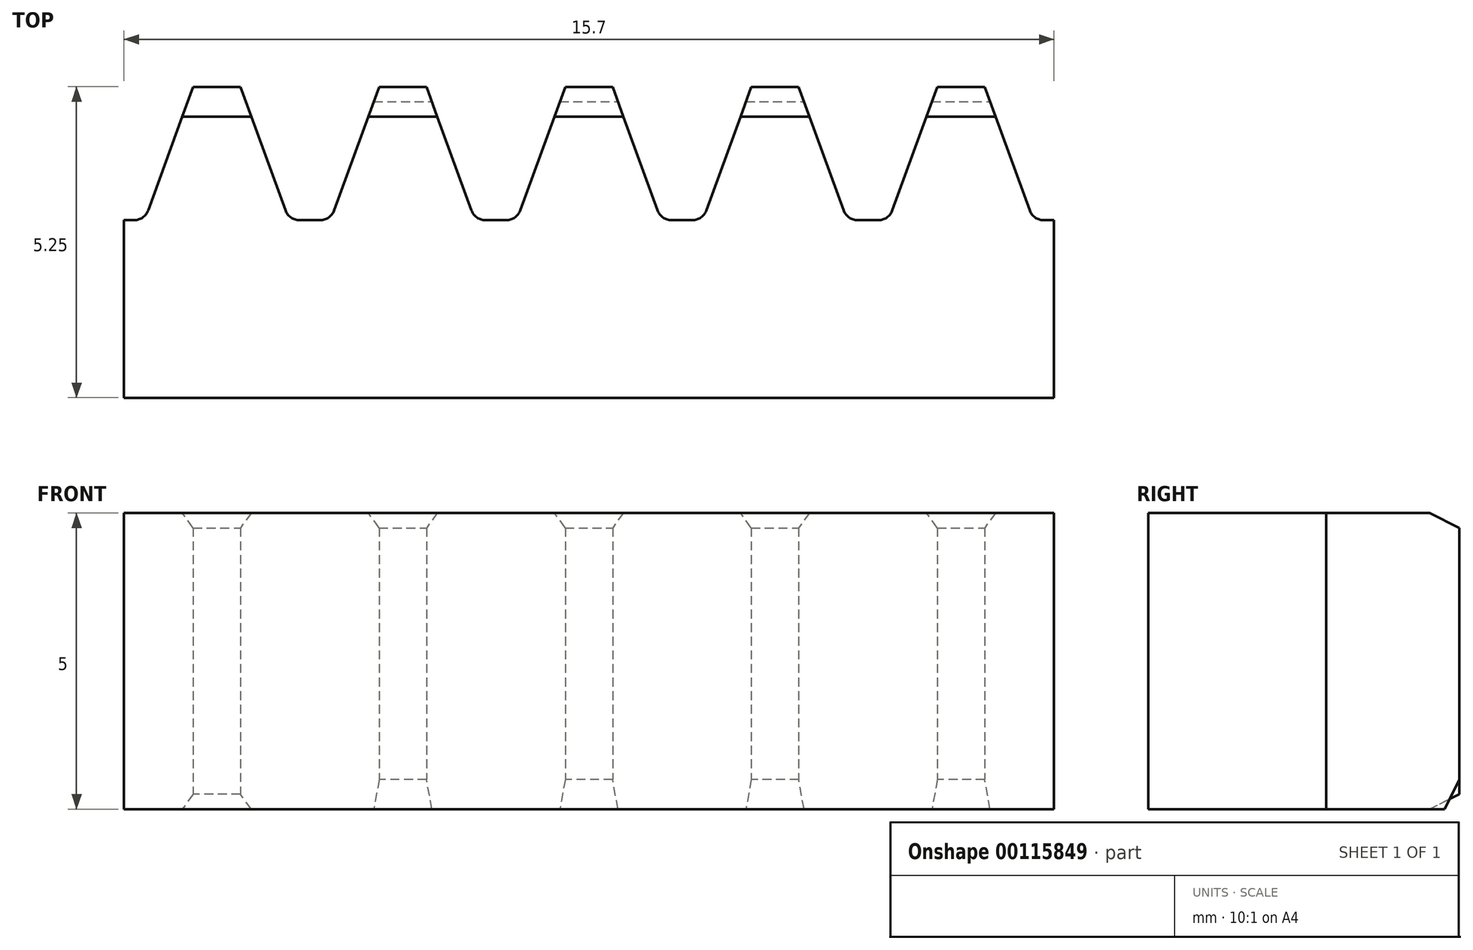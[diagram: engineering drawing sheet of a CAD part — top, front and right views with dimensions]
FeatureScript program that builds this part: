
annotation { "Feature Type Name" : "Feature", "Feature Type Description" : "" }
export const myFeature = defineFeature(function(context is Context, id is Id, definition is map)
    precondition{}
    {
        {
            var Q0;
            Q0=qCreatedBy(makeId("Top.planeOp"),FACE);
            var sketch = newSketch(context, id + "F0", { "sketchPlane" : qUnion([Q0])});
            skLineSegment(sketch, "E0", {"start": v(0.48, -14.18) * mm, "end": v(1.24, -12.1) * mm});
            skLineSegment(sketch, "E1", {"start": v(1.24, -12.1) * mm, "end": v(2.04, -12.1) * mm});
            skLineSegment(sketch, "E2", {"start": v(2.04, -12.1) * mm, "end": v(2.8, -14.18) * mm});
            skLineSegment(sketch, "E3", {"start": v(3.03, -14.34) * mm, "end": v(3.38, -14.34) * mm});
            skLineSegment(sketch, "E4", {"start": v(3.62, -14.18) * mm, "end": v(4.38, -12.1) * mm});
            skLineSegment(sketch, "E5", {"start": v(4.38, -12.1) * mm, "end": v(5.18, -12.1) * mm});
            skLineSegment(sketch, "E6", {"start": v(5.18, -12.1) * mm, "end": v(5.94, -14.18) * mm});
            skLineSegment(sketch, "E7", {"start": v(6.17, -14.34) * mm, "end": v(6.53, -14.34) * mm});
            skLineSegment(sketch, "E8", {"start": v(6.76, -14.18) * mm, "end": v(7.52, -12.1) * mm});
            skLineSegment(sketch, "E9", {"start": v(7.52, -12.1) * mm, "end": v(8.32, -12.1) * mm});
            skLineSegment(sketch, "E10", {"start": v(8.32, -12.1) * mm, "end": v(9.08, -14.18) * mm});
            skLineSegment(sketch, "E11", {"start": v(9.31, -14.34) * mm, "end": v(9.67, -14.34) * mm});
            skLineSegment(sketch, "E12", {"start": v(9.9, -14.18) * mm, "end": v(10.66, -12.1) * mm});
            skLineSegment(sketch, "E13", {"start": v(10.66, -12.1) * mm, "end": v(11.46, -12.1) * mm});
            skLineSegment(sketch, "E14", {"start": v(11.46, -12.1) * mm, "end": v(12.22, -14.18) * mm});
            skLineSegment(sketch, "E15", {"start": v(12.46, -14.34) * mm, "end": v(12.8, -14.34) * mm});
            skLineSegment(sketch, "E16", {"start": v(13.04, -14.18) * mm, "end": v(13.8, -12.1) * mm});
            skLineSegment(sketch, "E17", {"start": v(13.8, -12.1) * mm, "end": v(14.6, -12.1) * mm});
            skLineSegment(sketch, "E18", {"start": v(14.6, -12.1) * mm, "end": v(15.36, -14.18) * mm});
            skLineSegment(sketch, "E19", {"start": v(0.07, -14.34) * mm, "end": v(0.07, -17.34) * mm});
            skLineSegment(sketch, "E20", {"start": v(15.77, -14.34) * mm, "end": v(15.77, -17.34) * mm});
            skLineSegment(sketch, "E21", {"start": v(0.07, -14.34) * mm, "end": v(0.24, -14.34) * mm});
            skLineSegment(sketch, "E22", {"start": v(0.07, -17.34) * mm, "end": v(15.77, -17.34) * mm});
            skLineSegment(sketch, "E23", {"start": v(15.6, -14.34) * mm, "end": v(15.77, -14.34) * mm});
            skPoint(sketch, "E24.visualSharp", {"position": v(0.42, -14.34) * mm});
            skArc(sketch, "E24.filletArc", {"start": v(0.24, -14.34) * mm, "mid": v(0.39, -14.3) * mm, "end": v(0.48, -14.18) * mm});
            skPoint(sketch, "E25.visualSharp", {"position": v(2.86, -14.34) * mm});
            skArc(sketch, "E25.filletArc", {"start": v(2.8, -14.18) * mm, "mid": v(2.89, -14.3) * mm, "end": v(3.03, -14.34) * mm});
            skPoint(sketch, "E26.visualSharp", {"position": v(3.56, -14.34) * mm});
            skArc(sketch, "E26.filletArc", {"start": v(3.38, -14.34) * mm, "mid": v(3.53, -14.3) * mm, "end": v(3.62, -14.18) * mm});
            skPoint(sketch, "E27.visualSharp", {"position": v(6, -14.34) * mm});
            skArc(sketch, "E27.filletArc", {"start": v(5.94, -14.18) * mm, "mid": v(6.03, -14.3) * mm, "end": v(6.17, -14.34) * mm});
            skPoint(sketch, "E28.visualSharp", {"position": v(6.7, -14.34) * mm});
            skArc(sketch, "E28.filletArc", {"start": v(6.53, -14.34) * mm, "mid": v(6.67, -14.3) * mm, "end": v(6.76, -14.18) * mm});
            skPoint(sketch, "E29.visualSharp", {"position": v(9.14, -14.34) * mm});
            skArc(sketch, "E29.filletArc", {"start": v(9.08, -14.18) * mm, "mid": v(9.17, -14.3) * mm, "end": v(9.31, -14.34) * mm});
            skPoint(sketch, "E30.visualSharp", {"position": v(9.84, -14.34) * mm});
            skArc(sketch, "E30.filletArc", {"start": v(9.67, -14.34) * mm, "mid": v(9.81, -14.3) * mm, "end": v(9.9, -14.18) * mm});
            skPoint(sketch, "E31.visualSharp", {"position": v(12.28, -14.34) * mm});
            skArc(sketch, "E31.filletArc", {"start": v(12.22, -14.18) * mm, "mid": v(12.31, -14.3) * mm, "end": v(12.46, -14.34) * mm});
            skPoint(sketch, "E32.visualSharp", {"position": v(12.98, -14.34) * mm});
            skArc(sketch, "E32.filletArc", {"start": v(12.8, -14.34) * mm, "mid": v(12.95, -14.3) * mm, "end": v(13.04, -14.18) * mm});
            skPoint(sketch, "E33.visualSharp", {"position": v(15.42, -14.34) * mm});
            skArc(sketch, "E33.filletArc", {"start": v(15.36, -14.18) * mm, "mid": v(15.45, -14.3) * mm, "end": v(15.6, -14.34) * mm});
            skSolve(sketch);
        }
        {
            var Q0;
            Q0=makeQuery(id+"F0.imprint","IMPRINT",FACE,{"disambiguationData":[TD([[makeQuery(id+"F0.imprint","IMPRINT",EDGE,{"derivedFrom":sQuery(id+"F0.wireOp",EDGE,"E0")}),-1.0]])]});
            extrude(context, id + "F1", {"entities" : qUnion([Q0]), "depth" : 5 * mm});
        }
        {
            var Q0;
            Q0=makeQuery(id+"F1.opExtrude","CAP_EDGE",EDGE,{"disambiguationData":[OSD([sQuery(id+"F0.wireOp",EDGE,"E1")])],"isStart":false});
            var Q1;
            Q1=makeQuery(id+"F1.opExtrude","CAP_EDGE",EDGE,{"disambiguationData":[OSD([sQuery(id+"F0.wireOp",EDGE,"E5")])],"isStart":false});
            var Q2;
            Q2=makeQuery(id+"F1.opExtrude","CAP_EDGE",EDGE,{"disambiguationData":[OSD([sQuery(id+"F0.wireOp",EDGE,"E9")])],"isStart":false});
            var Q3;
            Q3=makeQuery(id+"F1.opExtrude","CAP_EDGE",EDGE,{"disambiguationData":[OSD([sQuery(id+"F0.wireOp",EDGE,"E13")])],"isStart":false});
            var Q4;
            Q4=makeQuery(id+"F1.opExtrude","CAP_EDGE",EDGE,{"disambiguationData":[OSD([sQuery(id+"F0.wireOp",EDGE,"E17")])],"isStart":false});
            var Q5;
            Q5=makeQuery(id+"F1.opExtrude","CAP_EDGE",EDGE,{"disambiguationData":[OSD([sQuery(id+"F0.wireOp",EDGE,"E17")])],"isStart":true});
            var Q6;
            Q6=makeQuery(id+"F1.opExtrude","CAP_EDGE",EDGE,{"disambiguationData":[OSD([sQuery(id+"F0.wireOp",EDGE,"E13")])],"isStart":true});
            var Q7;
            Q7=makeQuery(id+"F1.opExtrude","CAP_EDGE",EDGE,{"disambiguationData":[OSD([sQuery(id+"F0.wireOp",EDGE,"E9")])],"isStart":true});
            var Q8;
            Q8=makeQuery(id+"F1.opExtrude","CAP_EDGE",EDGE,{"disambiguationData":[OSD([sQuery(id+"F0.wireOp",EDGE,"E5")])],"isStart":true});
            var Q9;
            Q9=makeQuery(id+"F1.opExtrude","CAP_EDGE",EDGE,{"disambiguationData":[OSD([sQuery(id+"F0.wireOp",EDGE,"E1")])],"isStart":true});
            chamfer(context, id + "F2", {"entities" : qUnion([Q0, Q1, Q2, Q3, Q4, Q5, Q6, Q7, Q8, Q9]), "chamferType" : ChamferType.TWO_OFFSETS, "width1" : .25 * mm, "oppositeDirection" : false, "width2" : .5 * mm, "tangentPropagation" : true});
        }
    });
